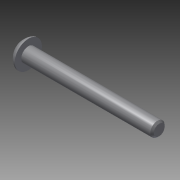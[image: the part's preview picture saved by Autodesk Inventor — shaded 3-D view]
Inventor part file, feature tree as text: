
AUTODESK INVENTOR PART (.ipt)
format: ipt  version: 2015 (Build 190159000, 159)  size: 118,272 bytes
history: native  units: in
note: dims shown in document units (in); Inventor stores cm internally (conversion verified against a paired STEP export)
features: other x3, extrude x1, chamfer x1, imported_body x1, sketch x1
ambient origin geometry x8: Origin, YZ Plane, XZ Plane, XY Plane, X Axis, Y Axis, Z Axis, Center Point
bodies: Body1 (feature_tree)
feature tree (7):
  other  "Bolt 1.5 inch"
  parser-record x1  (decoder bookkeeping rows leaked as tree rows — omitted from the tree; the rows remain in map.json)
  other  "Bolt"
  extrude  "thread length"  Depth=1.5in TaperAngle=0.0deg
  chamfer  "thread chamfer"  Distance=0.02in Angle=45.0deg
  imported_body  "Base1"
  sketch  "Sketch1"  dims[d0=0.164in d1=1.5in d2=0.0in d3=0.02in d4=0.125in d5=45.0deg d7=0.0in d9=0.0in]
